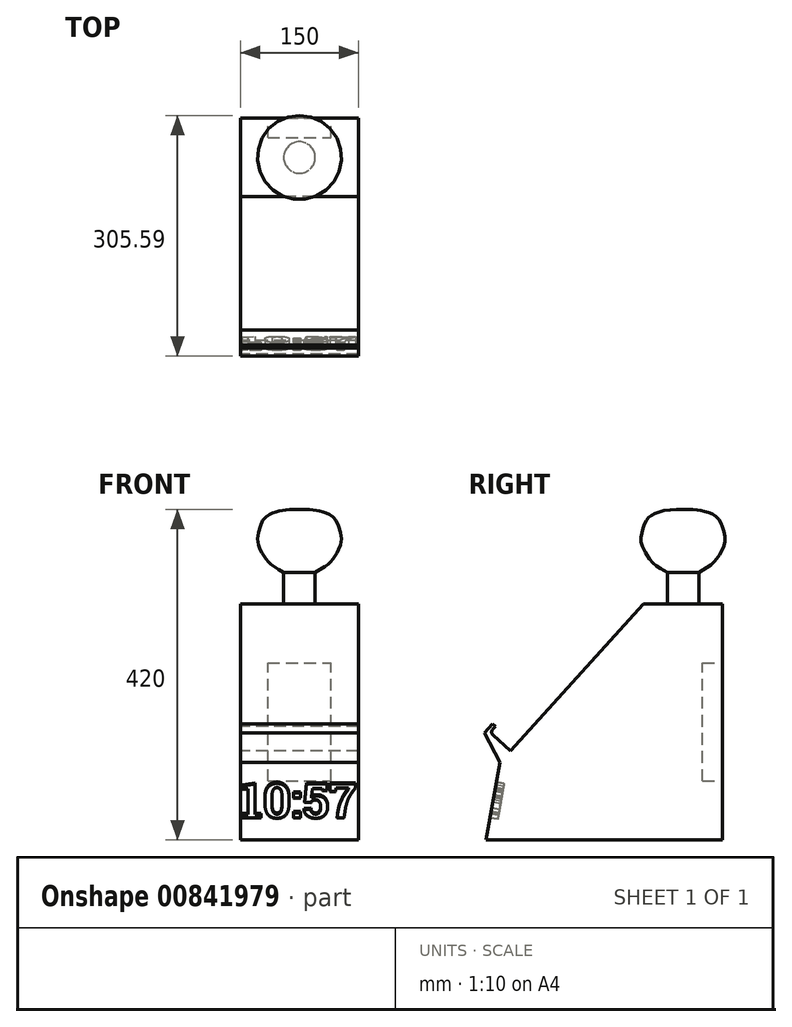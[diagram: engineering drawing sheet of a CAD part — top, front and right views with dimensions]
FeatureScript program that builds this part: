
annotation { "Feature Type Name" : "Feature", "Feature Type Description" : "" }
export const myFeature = defineFeature(function(context is Context, id is Id, definition is map)
    precondition{}
    {
        {
            var Q0;
            Q0=qCreatedBy(makeId("Right.planeOp"),FACE);
            var sketch = newSketch(context, id + "F0", { "sketchPlane" : qUnion([Q0])});
            skLineSegment(sketch, "E0", {"start": v(0, 0) * mm, "end": v(0, 300) * mm});
            skLineSegment(sketch, "E1", {"start": v(0, 0) * mm, "end": v(-300, 0) * mm});
            skLineSegment(sketch, "E2", {"start": v(-300, 0) * mm, "end": v(-282.64, 98.48) * mm});
            skLineSegment(sketch, "E3", {"start": v(-100, 300) * mm, "end": v(0, 300) * mm});
            skLineSegment(sketch, "E4", {"start": v(-282.64, 98.48) * mm, "end": v(0, 98.48) * mm});
            skLineSegment(sketch, "E5", {"start": v(-282.64, 98.48) * mm, "end": v(-100, 300) * mm});
            skLineSegment(sketch, "E6", {"start": v(-282.64, 98.48) * mm, "end": v(-269.2, 113.3) * mm});
            skLineSegment(sketch, "E7", {"start": v(-269.2, 113.3) * mm, "end": v(-298.84, 140.16) * mm});
            skLineSegment(sketch, "E8", {"start": v(-298.84, 140.16) * mm, "end": v(-282.64, 98.48) * mm});
            skLineSegment(sketch, "E9", {"start": v(-298.84, 140.16) * mm, "end": v(-292.13, 147.57) * mm});
            skLineSegment(sketch, "E10", {"start": v(-292.13, 147.57) * mm, "end": v(-288.42, 144.21) * mm});
            skLineSegment(sketch, "E11", {"start": v(-288.42, 144.21) * mm, "end": v(-291.78, 140.5) * mm});
            skLineSegment(sketch, "E12", {"start": v(-291.43, 133.45) * mm, "end": v(-269.2, 113.3) * mm});
            skPoint(sketch, "E13.visualSharp", {"position": v(-295.14, 136.8) * mm});
            skArc(sketch, "E13.filletArc", {"start": v(-291.78, 140.5) * mm, "mid": v(-293.07, 136.9) * mm, "end": v(-291.43, 133.45) * mm});
            skLineSegment(sketch, "E14", {"start": v(-298.84, 140.16) * mm, "end": v(-302.2, 136.46) * mm});
            skLineSegment(sketch, "E15", {"start": v(-302.2, 136.46) * mm, "end": v(-282.64, 98.48) * mm});
            skLineSegment(sketch, "E16", {"start": v(-291.43, 133.45) * mm, "end": v(-276.76, 104.96) * mm});
            skSolve(sketch);
        }
        {
            var Q0;
            {var subQ2=sQuery(id+"F0.wireOp",EDGE,"E1");Q0=makeQuery(id+"F0.imprint","IMPRINT",FACE,{"disambiguationData":[TD([[makeQuery(id+"F0.imprint","IMPRINT",EDGE,{"derivedFrom":subQ2}),-1.0]])]});}
            var Q1;
            {var subQ0=sQuery(id+"F0.wireOp",EDGE,"E9");Q1=makeQuery(id+"F0.imprint","IMPRINT",FACE,{"disambiguationData":[TD([[makeQuery(id+"F0.imprint","IMPRINT",EDGE,{"derivedFrom":subQ0}),-1.0]])]});}
            var Q2;
            Q2=makeQuery(id+"F0.imprint","IMPRINT",FACE,{"disambiguationData":[TD([[makeQuery(id+"F0.imprint","IMPRINT",EDGE,{"derivedFrom":sQuery(id+"F0.wireOp",EDGE,"E8")}),-1.0]])]});
            var Q3;
            {var subQ1=sQuery(id+"F0.wireOp",EDGE,"E3");Q3=makeQuery(id+"F0.imprint","IMPRINT",FACE,{"disambiguationData":[TD([[makeQuery(id+"F0.imprint","IMPRINT",EDGE,{"derivedFrom":subQ1}),-1.0]])]});}
            var Q4;
            {var subQ0=sQuery(id+"F0.wireOp",EDGE,"E8");Q4=makeQuery(id+"F0.imprint","IMPRINT",FACE,{"disambiguationData":[TD([[makeQuery(id+"F0.imprint","IMPRINT",EDGE,{"derivedFrom":subQ0}),1.0]])]});}
            var Q5;
            {var subQ3=sQuery(id+"F0.wireOp",EDGE,"E16");Q5=makeQuery(id+"F0.imprint","IMPRINT",FACE,{"disambiguationData":[TD([[makeQuery(id+"F0.imprint","IMPRINT",EDGE,{"derivedFrom":subQ3}),1.0]])]});}
            extrude(context, id + "F1", {"entities" : qUnion([Q0, Q1, Q2, Q3, Q4, Q5]), "endBound" : BoundingType.SYMMETRIC, "depth" : 150 * mm, "offsetDistance" : 25 * mm});
        }
        {
            var Q0;
            Q0=qCreatedBy(makeId("Right.planeOp"),FACE);
            var sketch = newSketch(context, id + "F2", { "sketchPlane" : qUnion([Q0])});
            skLineSegment(sketch, "E17", {"start": v(0, 0) * mm, "end": v(0, 300) * mm});
            skLineSegment(sketch, "E18", {"start": v(0, 300) * mm, "end": v(-50, 300) * mm});
            skLineSegment(sketch, "E19", {"start": v(-50, 300) * mm, "end": v(-50, 340) * mm});
            skLineSegment(sketch, "E20", {"start": v(-50, 340) * mm, "end": v(-30, 340) * mm});
            skLineSegment(sketch, "E21", {"start": v(-30, 340) * mm, "end": v(-30, 300) * mm});
            skLineSegment(sketch, "E22", {"start": v(-50, 340) * mm, "end": v(-50, 420) * mm});
            skFitSpline(sketch, "E23", {"points": [v(-30, 340) * mm, v(-14.21, 349.84) * mm, v(-4.24, 361.89) * mm, v(3.24, 379.75) * mm, v(0, 398.23) * mm, v(-6.9, 410.33) * mm, v(-19.81, 416.97) * mm, v(-32.3, 419.44) * mm, v(-50, 420) * mm], "startDerivative": vector(118.25, 73.32) * mm, "endDerivative": vector(-175.6, 4.25) * mm});
            skSolve(sketch);
        }
        {
            var Q0;
            Q0=makeQuery(id+"F2.imprint","IMPRINT",FACE,{"disambiguationData":[TD([[makeQuery(id+"F2.imprint","IMPRINT",EDGE,{"derivedFrom":sQuery(id+"F2.wireOp",EDGE,"E20")}),1.0]])]});
            var Q1;
            {var subQ0=sQuery(id+"F2.wireOp",EDGE,"E19");Q1=makeQuery(id+"F2.imprint","IMPRINT",FACE,{"disambiguationData":[TD([[makeQuery(id+"F2.imprint","IMPRINT",EDGE,{"derivedFrom":subQ0}),-1.0]])]});}
            var Q2;
            Q2=sQuery(id+"F2.wireOp",EDGE,"E19");
            revolve(context, id + "F3", {"operationType" : NewBodyOperationType.ADD, "surfaceOperationType" : NewSurfaceOperationType.NEW, "entities" : qUnion([Q0, Q1]), "axis" : qUnion([Q2]), "revolveType" : RevolveType.FULL});
        }
        {
            var Q0;
            Q0=makeQuery(id+"F1.opExtrude","SWEPT_FACE",FACE,{"disambiguationData":[OSD([sQuery(id+"F0.wireOp",EDGE,"E2")])]});
            var sketch = newSketch(context, id + "F4", { "sketchPlane" : qUnion([Q0])});
            skLineSegment(sketch, "E24", {"start": v(0, -52.1) * mm, "end": v(0, 47.9) * mm});
            skText(sketch, "E25", { "text": "10:57", "fontName": "RobotoSlab-Bold.ttf"});
            const initialGuessF4  = {"E25": [-0.075, -0.02327, 1, 0, 0.04584]};
            skSetInitialGuess(sketch, initialGuessF4);
            skSolve(sketch);
        }
        {
            var Q0;
            Q0 = qSketchRegion(id + "F4", true);
            extrude(context, id + "F5", {"entities" : qUnion([Q0]), "operationType" : NewBodyOperationType.REMOVE, "oppositeDirection" : true, "depth" : 10 * mm, "offsetDistance" : 25 * mm});
        }
        {
            var Q0;
            Q0=makeQuery(id+"F1.opExtrude","SWEPT_FACE",FACE,{"disambiguationData":[OSD([sQuery(id+"F0.wireOp",EDGE,"E0")])]});
            var sketch = newSketch(context, id + "F6", { "sketchPlane" : qUnion([Q0])});
            skLineSegment(sketch, "E26.bottom", {"start": v(40, 75) * mm, "end": v(-40, 75) * mm});
            skLineSegment(sketch, "E26.top", {"start": v(40, 225) * mm, "end": v(-40, 225) * mm});
            skLineSegment(sketch, "E26.left", {"start": v(40, 75) * mm, "end": v(40, 225) * mm});
            skLineSegment(sketch, "E26.right", {"start": v(-40, 75) * mm, "end": v(-40, 225) * mm});
            skPoint(sketch, "E26.middle", {"position": v(0, 150) * mm});
            skPoint(sketch, "E26.middle.positionSnap0", {"position": v(-75, 150) * mm});
            skPoint(sketch, "E26.centerSnap0", {"position": v(-75, 150) * mm});
            skSolve(sketch);
        }
        {
            var Q0;
            Q0 = qSketchRegion(id + "F6", true);
            extrude(context, id + "F7", {"entities" : qUnion([Q0]), "operationType" : NewBodyOperationType.REMOVE, "oppositeDirection" : true, "depth" : 25 * mm, "offsetDistance" : 25 * mm});
        }
    });
